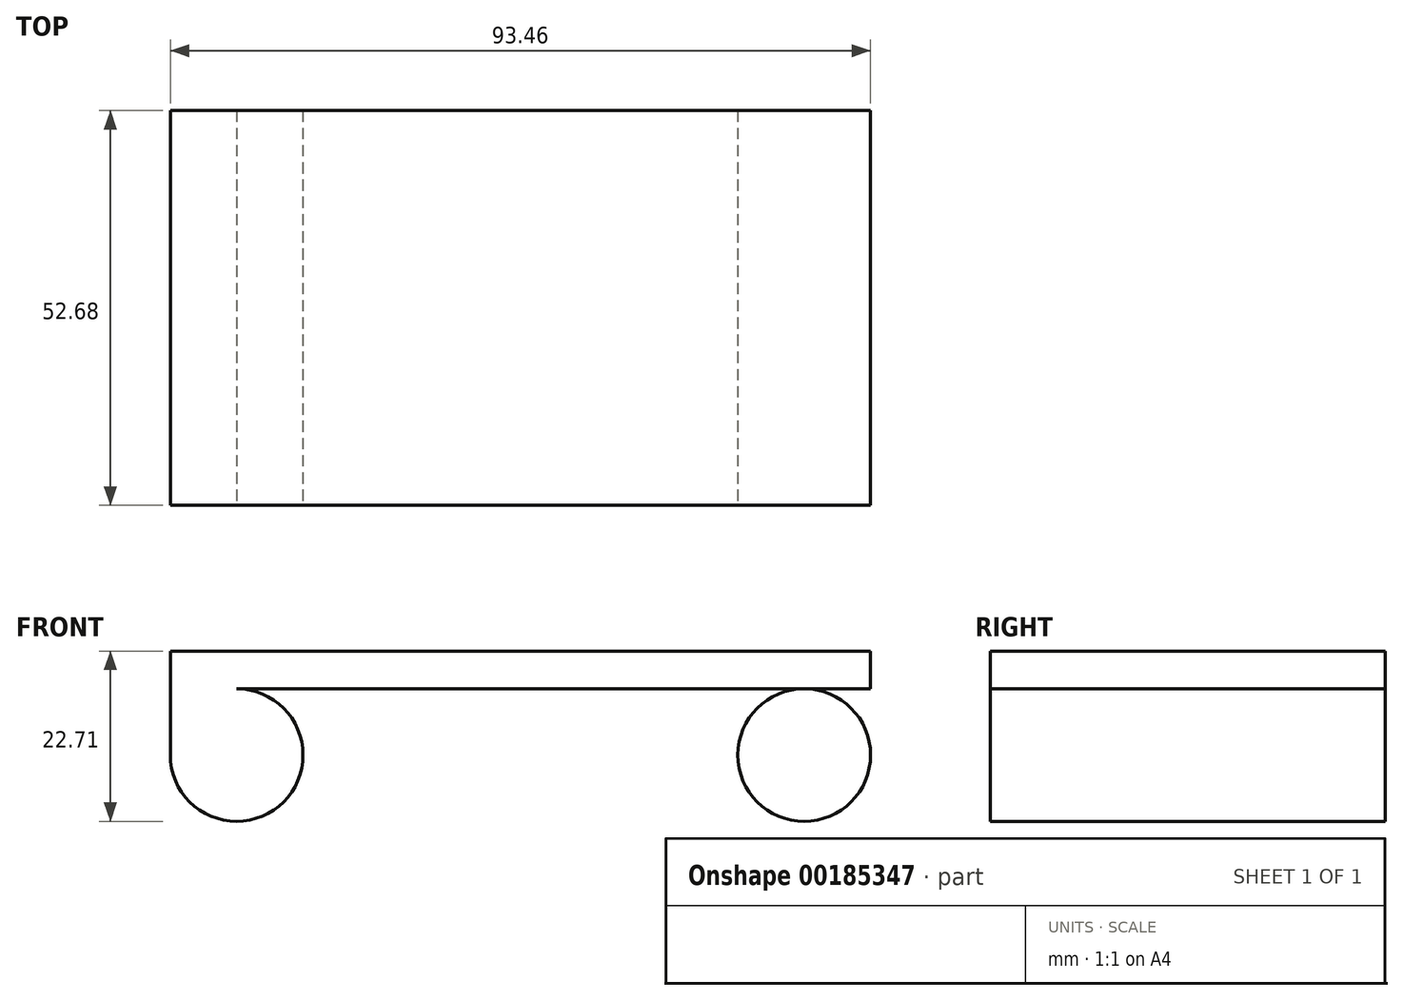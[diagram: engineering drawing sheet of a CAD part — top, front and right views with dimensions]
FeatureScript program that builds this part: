
annotation { "Feature Type Name" : "Feature", "Feature Type Description" : "" }
export const myFeature = defineFeature(function(context is Context, id is Id, definition is map)
    precondition{}
    {
        {
            var Q0;
            Q0=qCreatedBy(makeId("Top.planeOp"),FACE);
            var sketch = newSketch(context, id + "F0", { "sketchPlane" : qUnion([Q0])});
            skLineSegment(sketch, "E0.bottom", {"start": v(46.73, -26.34) * mm, "end": v(-46.73, -26.34) * mm});
            skLineSegment(sketch, "E0.top", {"start": v(46.73, 26.34) * mm, "end": v(-46.73, 26.34) * mm});
            skLineSegment(sketch, "E0.left", {"start": v(46.73, -26.34) * mm, "end": v(46.73, 26.34) * mm});
            skLineSegment(sketch, "E0.right", {"start": v(-46.73, -26.34) * mm, "end": v(-46.73, 26.34) * mm});
            skPoint(sketch, "E0.middle", {"position": v(0, 0) * mm});
            skSolve(sketch);
        }
        {
            var Q0;
            Q0=makeQuery(id+"F0.imprint","IMPRINT",FACE,{"disambiguationData":[TD([[makeQuery(id+"F0.imprint","IMPRINT",EDGE,{"derivedFrom":sQuery(id+"F0.wireOp",EDGE,"E0.bottom")}),-1.0]])]});
            extrude(context, id + "F1", {"entities" : qUnion([Q0]), "depth" : 5 * mm, "offsetDistance" : 25 * mm});
        }
        {
            var Q0;
            Q0=makeQuery(id+"F1.opExtrude","SWEPT_FACE",FACE,{"disambiguationData":[OSD([sQuery(id+"F0.wireOp",EDGE,"E0.bottom")])]});
            var sketch = newSketch(context, id + "F2", { "sketchPlane" : qUnion([Q0])});
            skCircle(sketch, "E1", {"center": v(-37.87, -8.86) * mm, "radius": 8.86 * mm});
            skLineSegment(sketch, "E2", {"start": v(-46.73, 0) * mm, "end": v(-46.73, -26.41) * mm});
            skLineSegment(sketch, "E3", {"start": v(0, 0) * mm, "end": v(0, -26.7) * mm});
            skCircle(sketch, "E4.MirrorC", {"center": v(37.87, -8.86) * mm, "radius": 8.86 * mm});
            skLineSegment(sketch, "E5.MirrorCS", {"start": v(46.73, 0) * mm, "end": v(46.73, -26.41) * mm});
            skSolve(sketch);
        }
        {
            var Q0;
            {var subQ0=sQuery(id+"F2.wireOp",EDGE,"E1");var subQ1=makeQuery(id+"F2.imprint","INTERSECT",VERTEX,{"derivedFrom":[subQ0,sQuery(id+"F2.wireOp",EDGE,"E2")]});Q0=makeQuery(id+"FUMatKnndqB00uI_1.imprint","IMPRINT",FACE,{"disambiguationData":[TD([[makeQuery(id+"FUMatKnndqB00uI_1.imprint","IMPRINT",EDGE,{"derivedFrom":makeQuery(id+"F2.imprint","IMPRINT",EDGE,{"disambiguationData":[TD([[subQ1,1.0]])],"derivedFrom":subQ0})}),1.0]])]});}
            var Q1;
            {var subQ0=sQuery(id+"F2.wireOp",EDGE,"E2");var subQ1=sQuery(id+"F2.wireOp",EDGE,"E1");var subQ2=makeQuery(id+"F2.imprint","INTERSECT",VERTEX,{"derivedFrom":[subQ1,subQ0]});Q1=makeQuery(id+"F2.imprint","IMPRINT",FACE,{"disambiguationData":[TD([[makeQuery(id+"F2.imprint","IMPRINT",EDGE,{"disambiguationData":[TD([[subQ2,1.0]])],"derivedFrom":subQ1}),-1.0]])]});}
            var Q2;
            {var subQ0=sQuery(id+"F2.wireOp",EDGE,"E4.MirrorC");var subQ1=makeQuery(id+"F2.imprint","INTERSECT",VERTEX,{"derivedFrom":[subQ0,sQuery(id+"F2.wireOp",EDGE,"E5.MirrorCS")]});Q2=makeQuery(id+"F2.imprint","IMPRINT",FACE,{"disambiguationData":[TD([[makeQuery(id+"F2.imprint","IMPRINT",EDGE,{"disambiguationData":[TD([[subQ1,1.0]])],"derivedFrom":subQ0}),-1.0]])]});}
            var Q3;
            {var subQ0=sQuery(id+"F2.wireOp",EDGE,"E1");var subQ1=makeQuery(id+"F2.imprint","INTERSECT",VERTEX,{"derivedFrom":[subQ0,sQuery(id+"F2.wireOp",EDGE,"E2")]});Q3=makeQuery(id+"F2.imprint","IMPRINT",FACE,{"disambiguationData":[TD([[makeQuery(id+"F2.imprint","IMPRINT",EDGE,{"disambiguationData":[TD([[subQ1,1.0]])],"derivedFrom":subQ0}),1.0]])]});}
            var Q4;
            {var subQ0=sQuery(id+"F2.wireOp",EDGE,"E5.MirrorCS");var subQ1=sQuery(id+"F2.wireOp",EDGE,"E4.MirrorC");var subQ2=makeQuery(id+"F2.imprint","INTERSECT",VERTEX,{"derivedFrom":[subQ1,subQ0]});Q4=makeQuery(id+"F2.imprint","IMPRINT",FACE,{"disambiguationData":[TD([[makeQuery(id+"F2.imprint","IMPRINT",EDGE,{"disambiguationData":[TD([[subQ2,1.0]])],"derivedFrom":subQ1}),1.0]])]});}
            var Q5;
            Q5=makeQuery(id+"F1.opExtrude","SWEPT_FACE",FACE,{"disambiguationData":[OSD([sQuery(id+"F0.wireOp",EDGE,"E0.top")])]});
            extrude(context, id + "F3", {"entities" : qUnion([Q0, Q1, Q2, Q3, Q4]), "operationType" : NewBodyOperationType.ADD, "endBound" : BoundingType.UP_TO_SURFACE, "oppositeDirection" : true, "depth" : 25 * mm, "endBoundEntityFace" : qUnion([Q5]), "offsetDistance" : 25 * mm});
        }
    });
